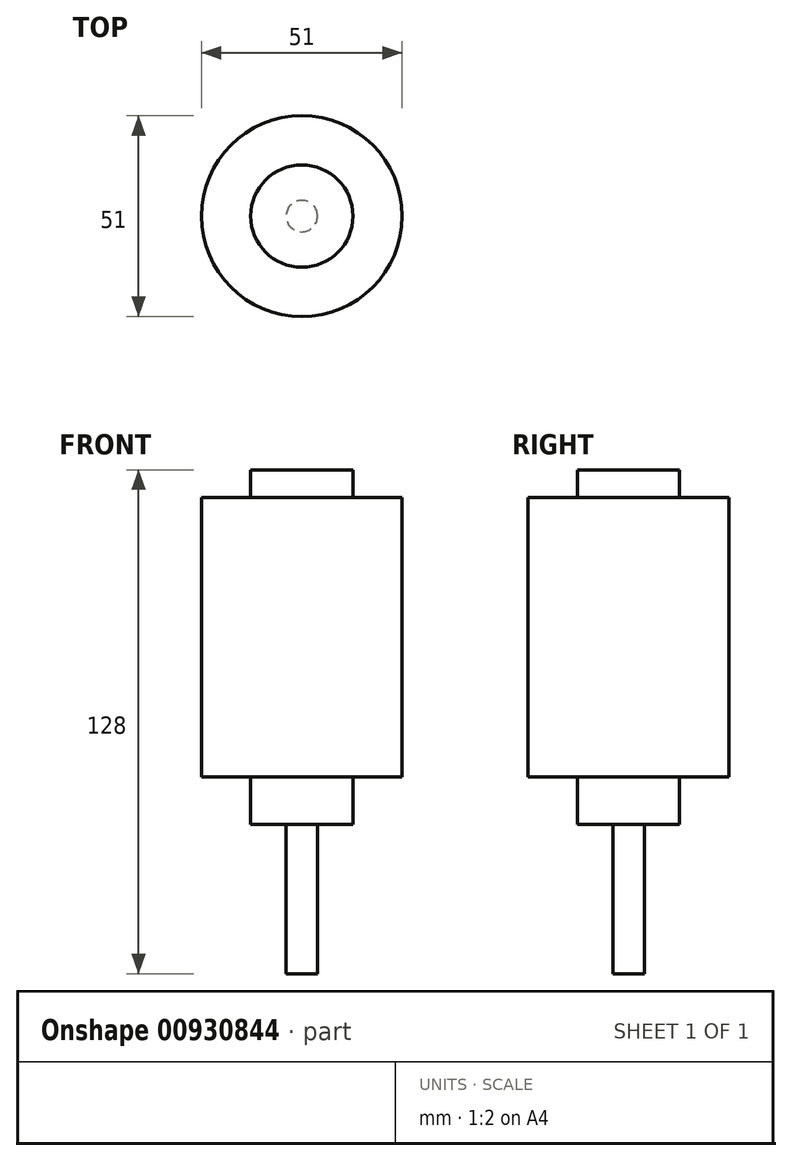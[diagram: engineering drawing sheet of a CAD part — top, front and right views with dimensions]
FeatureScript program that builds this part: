
annotation { "Feature Type Name" : "Feature", "Feature Type Description" : "" }
export const myFeature = defineFeature(function(context is Context, id is Id, definition is map)
    precondition{}
    {
        {
            var Q0;
            Q0=qCreatedBy(makeId("Top.planeOp"),FACE);
            var sketch = newSketch(context, id + "F0", { "sketchPlane" : qUnion([Q0])});
            skCircle(sketch, "E0", {"center": v(0, 0) * mm, "radius": 4 * mm});
            skSolve(sketch);
        }
        {
            var Q0;
            Q0=makeQuery(id+"F0.imprint","IMPRINT",FACE,{"disambiguationData":[TD([[makeQuery(id+"F0.imprint","IMPRINT",EDGE,{"derivedFrom":sQuery(id+"F0.wireOp",EDGE,"E0")}),1.0]])]});
            extrude(context, id + "F1", {"entities" : qUnion([Q0]), "depth" : 38 * mm, "offsetDistance" : 25 * mm});
        }
        {
            var Q0;
            Q0=makeQuery(id+"F1.opExtrude","CAP_FACE",FACE,{"disambiguationData":[OSD([sQuery(id+"F0.wireOp",EDGE,"E0")])],"isStart":false});
            var sketch = newSketch(context, id + "F2", { "sketchPlane" : qUnion([Q0])});
            skCircle(sketch, "E1", {"center": v(0, 0) * mm, "radius": 13 * mm});
            skSolve(sketch);
        }
        {
            var Q0;
            Q0=makeQuery(id+"F2.imprint","IMPRINT",FACE,{"disambiguationData":[TD([[makeQuery(id+"F2.imprint","IMPRINT",EDGE,{"derivedFrom":sQuery(id+"F2.wireOp",EDGE,"E1")}),1.0]])]});
            var Q1;
            Q1=makeQuery(id+"F2.imprint","IMPRINT",FACE,{"disambiguationData":[TD([[makeQuery(id+"F2.imprint","IMPRINT",EDGE,{"derivedFrom":makeQuery(id+"F1.opExtrude","CAP_EDGE",EDGE,{"disambiguationData":[OSD([sQuery(id+"F0.wireOp",EDGE,"E0")])],"isStart":false})}),1.0]])]});
            extrude(context, id + "F3", {"entities" : qUnion([Q0, Q1]), "operationType" : NewBodyOperationType.ADD, "depth" : 12 * mm, "offsetDistance" : 25 * mm});
        }
        {
            var Q0;
            Q0=makeQuery(id+"F3.opExtrude","CAP_FACE",FACE,{"disambiguationData":[OSD([sQuery(id+"F2.wireOp",EDGE,"E1")])],"isStart":false});
            var sketch = newSketch(context, id + "F4", { "sketchPlane" : qUnion([Q0])});
            skCircle(sketch, "E2", {"center": v(0, 0) * mm, "radius": 25.5 * mm});
            skSolve(sketch);
        }
        {
            var Q0;
            Q0=makeQuery(id+"F4.imprint","IMPRINT",FACE,{"disambiguationData":[TD([[makeQuery(id+"F4.imprint","IMPRINT",EDGE,{"derivedFrom":sQuery(id+"F4.wireOp",EDGE,"E2")}),1.0]])]});
            var Q1;
            Q1=makeQuery(id+"F4.imprint","IMPRINT",FACE,{"disambiguationData":[TD([[makeQuery(id+"F4.imprint","IMPRINT",EDGE,{"derivedFrom":makeQuery(id+"F3.opExtrude","CAP_EDGE",EDGE,{"disambiguationData":[OSD([sQuery(id+"F2.wireOp",EDGE,"E1")])],"isStart":false})}),1.0]])]});
            extrude(context, id + "F5", {"entities" : qUnion([Q0, Q1]), "operationType" : NewBodyOperationType.ADD, "depth" : 71 * mm, "offsetDistance" : 25 * mm});
        }
        {
            var Q0;
            Q0=makeQuery(id+"F5.opExtrude","CAP_FACE",FACE,{"disambiguationData":[OSD([sQuery(id+"F4.wireOp",EDGE,"E2")])],"isStart":false});
            var sketch = newSketch(context, id + "F6", { "sketchPlane" : qUnion([Q0])});
            skCircle(sketch, "E3", {"center": v(0, 0) * mm, "radius": 13 * mm});
            skSolve(sketch);
        }
        {
            var Q0;
            Q0=makeQuery(id+"F6.imprint","IMPRINT",FACE,{"disambiguationData":[TD([[makeQuery(id+"F6.imprint","IMPRINT",EDGE,{"derivedFrom":sQuery(id+"F6.wireOp",EDGE,"E3")}),1.0]])]});
            extrude(context, id + "F7", {"entities" : qUnion([Q0]), "operationType" : NewBodyOperationType.ADD, "depth" : 7 * mm, "offsetDistance" : 25 * mm});
        }
    });
